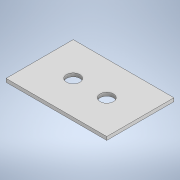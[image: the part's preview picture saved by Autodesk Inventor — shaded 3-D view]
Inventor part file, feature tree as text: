
AUTODESK INVENTOR PART (.ipt)
format: ipt  version: 2020.2 (Build 242310000, 310)  size: 98,304 bytes
history: native  units: in
note: dims shown in document units (in); Inventor stores cm internally (conversion verified against a paired STEP export)
features: extrude x1, sketch x1
ambient origin geometry x8: Origin, YZ Plane, XZ Plane, XY Plane, X Axis, Y Axis, Z Axis, Center Point
bodies: Solid1 (feature_tree)
feature tree (2):
  extrude  "Extrusion1"  Depth=0.7874in
  sketch  "Sketch1"  dims[d0=1.1811in d1=0.7874in d2=0.1575in d3=0.1575in d4=0.0394in d5=0.0in]
